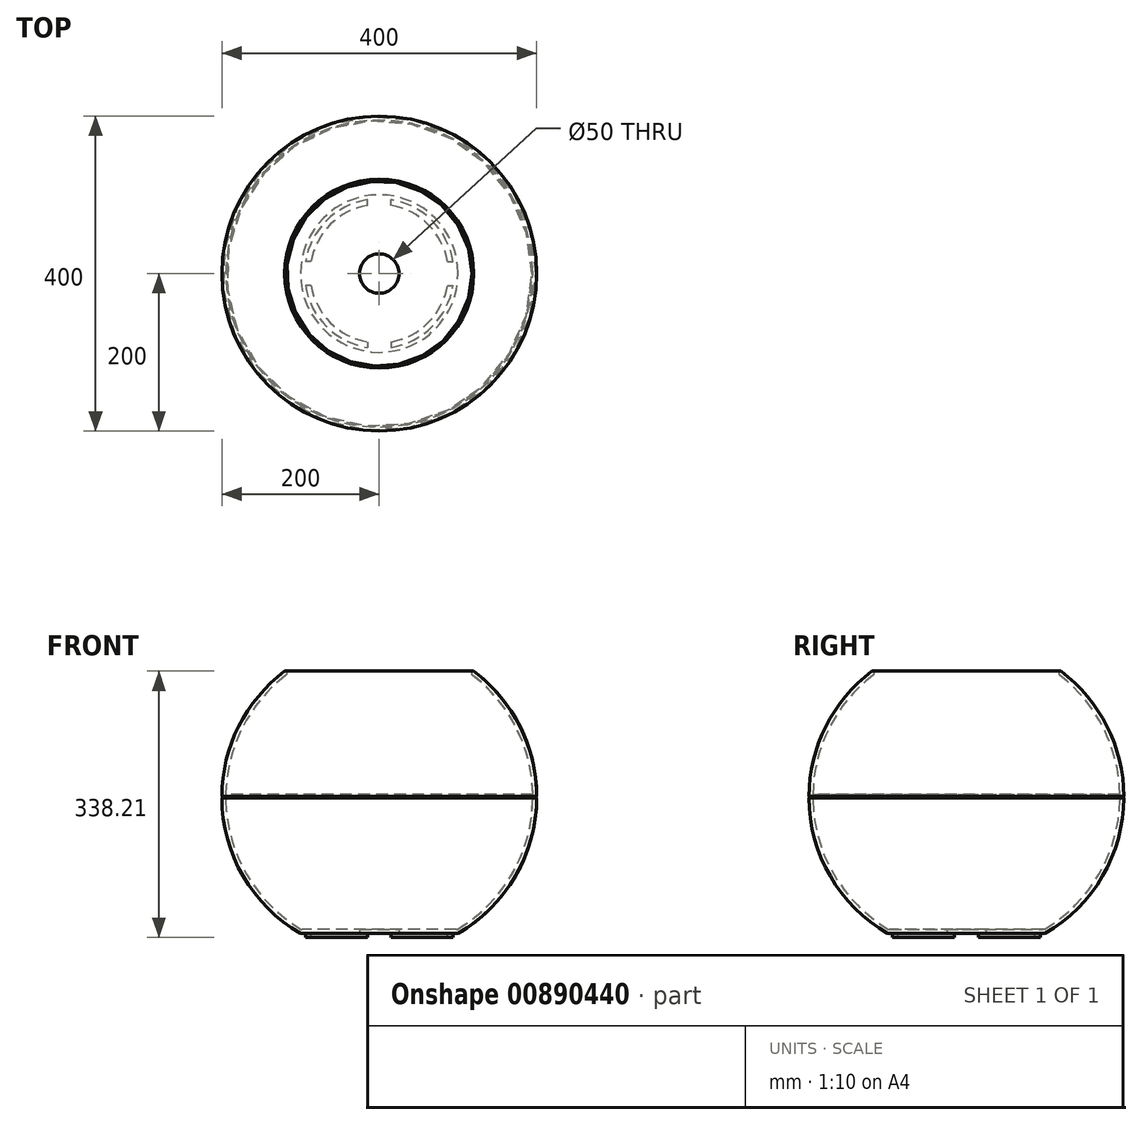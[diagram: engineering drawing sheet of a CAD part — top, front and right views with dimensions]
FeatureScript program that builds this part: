
annotation { "Feature Type Name" : "Feature", "Feature Type Description" : "" }
export const myFeature = defineFeature(function(context is Context, id is Id, definition is map)
    precondition{}
    {
        {
            var Q0;
            Q0=qCreatedBy(makeId("Front.planeOp"),FACE);
            var sketch = newSketch(context, id + "F0", { "sketchPlane" : qUnion([Q0])});
            skArc(sketch, "E0", {"start": v(100, 0) * mm, "mid": v(172.95, 72.77) * mm, "end": v(200, 172.2) * mm});
            skLineSegment(sketch, "E1", {"start": v(0, 333.2) * mm, "end": v(120, 333.2) * mm});
            skLineSegment(sketch, "E2", {"start": v(0, 0) * mm, "end": v(100, 0) * mm});
            skLineSegment(sketch, "E3", {"start": v(0, 333.2) * mm, "end": v(0, 0) * mm});
            skPoint(sketch, "E4.orphan", {"position": v(-120, 333.2) * mm});
            skPoint(sketch, "E5.orphan", {"position": v(-100, 0) * mm});
            skArc(sketch, "E6", {"start": v(200, 174.2) * mm, "mid": v(199, 173.2) * mm, "end": v(200, 172.2) * mm});
            skArc(sketch, "E7.trimOffspring", {"start": v(200, 174.2) * mm, "mid": v(178.66, 263.1) * mm, "end": v(120, 333.2) * mm});
            skSolve(sketch);
        }
        {
            var Q0;
            Q0=makeQuery(id+"F0.imprint","IMPRINT",FACE,{"disambiguationData":[TD([[makeQuery(id+"F0.imprint","IMPRINT",EDGE,{"derivedFrom":sQuery(id+"F0.wireOp",EDGE,"E0")}),1.0]])]});
            var Q1;
            Q1=sQuery(id+"F0.wireOp",EDGE,"E3");
            revolve(context, id + "F1", {"surfaceOperationType" : NewSurfaceOperationType.NEW, "entities" : qUnion([Q0]), "axis" : qUnion([Q1]), "revolveType" : RevolveType.FULL});
        }
        {
            var Q0;
            Q0=makeQuery(id+"F1.opRevolve","SWEPT_FACE",FACE,{"disambiguationData":[OSD([sQuery(id+"F0.wireOp",EDGE,"E1")])]});
            shell(context, id + "F2", {"entities" : qUnion([Q0]), "thickness" : 5 * mm});
        }
        {
            var Q0;
            Q0=makeQuery(id+"F2.opShell","OFFSET_EDGE",EDGE,{"disambiguationData":[OSD([sQuery(id+"F0.wireOp",EDGE,"E0"),sQuery(id+"F0.wireOp",EDGE,"E1")])]});
            fillet(context, id + "F3", {"entities" : qUnion([Q0]), "radius" : 3 * mm, "tangentPropagation" : true, "allowEdgeOverflow" : false});
        }
        {
            var Q0;
            Q0=makeQuery(id+"F1.opRevolve","SWEPT_FACE",FACE,{"disambiguationData":[OSD([sQuery(id+"F0.wireOp",EDGE,"E2")])]});
            var sketch = newSketch(context, id + "F4", { "sketchPlane" : qUnion([Q0])});
            skCircle(sketch, "E8", {"center": v(0, 0) * mm, "radius": 25 * mm});
            skSolve(sketch);
        }
        {
            var Q0;
            Q0=makeQuery(id+"F4.imprint","IMPRINT",FACE,{"disambiguationData":[TD([[makeQuery(id+"F4.imprint","IMPRINT",EDGE,{"derivedFrom":sQuery(id+"F4.wireOp",EDGE,"E8")}),1.0]])]});
            extrude(context, id + "F5", {"entities" : qUnion([Q0]), "operationType" : NewBodyOperationType.REMOVE, "oppositeDirection" : true, "depth" : 5 * mm, "offsetDistance" : 25 * mm});
        }
        {
            var Q0;
            Q0=makeQuery(id+"F1.opRevolve","SWEPT_FACE",FACE,{"disambiguationData":[OSD([sQuery(id+"F0.wireOp",EDGE,"E2")])]});
            var sketch = newSketch(context, id + "F6", { "sketchPlane" : qUnion([Q0])});
            skArc(sketch, "E9.0", {"start": v(93.8, -15) * mm, "mid": v(67.18, -67.18) * mm, "end": v(15, -93.8) * mm});
            skArc(sketch, "E10.0", {"start": v(86.71, -15) * mm, "mid": v(62.23, -62.23) * mm, "end": v(15, -86.71) * mm});
            skLineSegment(sketch, "E11", {"start": v(86.71, 15) * mm, "end": v(93.8, 15) * mm});
            skLineSegment(sketch, "E12", {"start": v(86.71, -15) * mm, "end": v(93.8, -15) * mm});
            skLineSegment(sketch, "E13.1.0", {"start": v(15, 86.71) * mm, "end": v(15, 93.8) * mm});
            skLineSegment(sketch, "E13.1.1", {"start": v(-15, 86.71) * mm, "end": v(-15, 93.8) * mm});
            skLineSegment(sketch, "E13.2.0", {"start": v(-86.71, 15) * mm, "end": v(-93.8, 15) * mm});
            skLineSegment(sketch, "E13.2.1", {"start": v(-86.71, -15) * mm, "end": v(-93.8, -15) * mm});
            skLineSegment(sketch, "E13.3.0", {"start": v(-15, -86.71) * mm, "end": v(-15, -93.8) * mm});
            skLineSegment(sketch, "E13.3.1", {"start": v(15, -86.71) * mm, "end": v(15, -93.8) * mm});
            skArc(sketch, "E14.trimOffspring", {"start": v(-15, -86.71) * mm, "mid": v(-62.23, -62.23) * mm, "end": v(-86.71, -15) * mm});
            skArc(sketch, "E15.trimOffspring", {"start": v(-15, -93.8) * mm, "mid": v(-67.18, -67.18) * mm, "end": v(-93.8, -15) * mm});
            skArc(sketch, "E16.trimOffspring", {"start": v(-86.71, 15) * mm, "mid": v(-62.23, 62.23) * mm, "end": v(-15, 86.71) * mm});
            skArc(sketch, "E17.trimOffspring", {"start": v(-93.8, 15) * mm, "mid": v(-67.18, 67.18) * mm, "end": v(-15, 93.8) * mm});
            skArc(sketch, "E18.trimOffspring", {"start": v(15, 86.71) * mm, "mid": v(62.23, 62.23) * mm, "end": v(86.71, 15) * mm});
            skArc(sketch, "E19.trimOffspring", {"start": v(15, 93.8) * mm, "mid": v(67.18, 67.18) * mm, "end": v(93.8, 15) * mm});
            skSolve(sketch);
        }
        {
            var Q0;
            Q0 = qSketchRegion(id + "F6", true);
            extrude(context, id + "F7", {"entities" : qUnion([Q0]), "operationType" : NewBodyOperationType.ADD, "depth" : 5 * mm, "offsetDistance" : 25 * mm});
        }
    });
